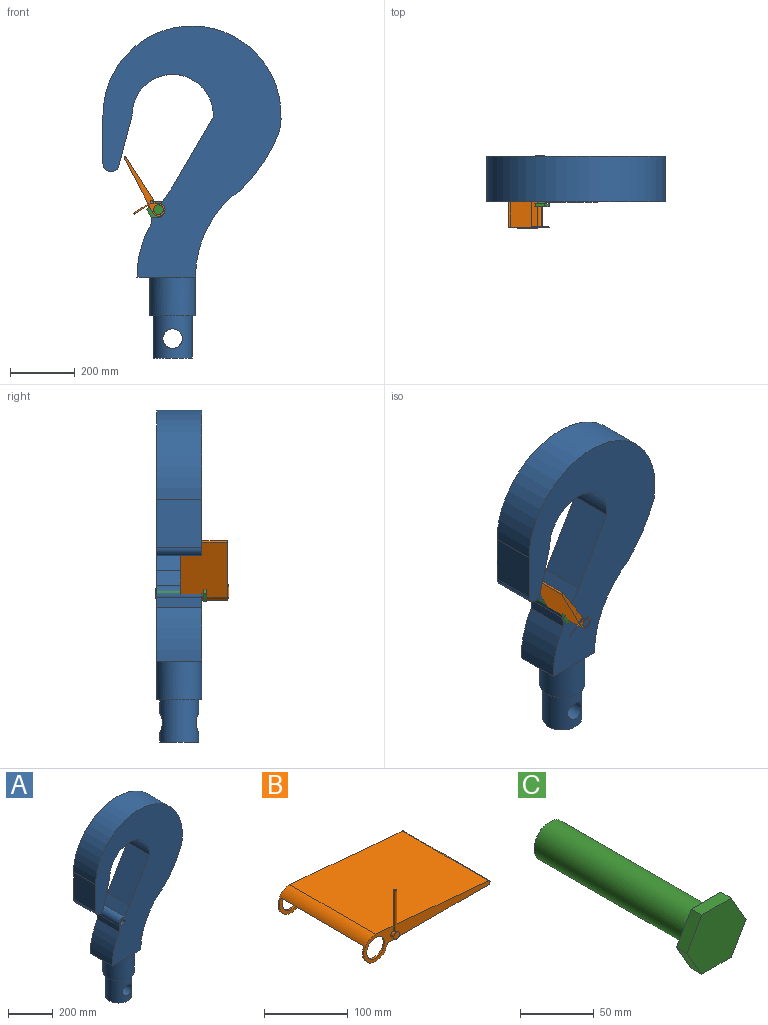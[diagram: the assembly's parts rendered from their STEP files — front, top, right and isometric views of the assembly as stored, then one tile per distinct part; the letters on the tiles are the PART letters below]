
ASSEMBLY  parts=3 mates=2
PART A: 26 faces, bbox 550x140x1025 mm
  f0: cylinder r=60mm len=130mm, axis (0,0,1), area 43158mm2, adj f2,f3,f24
  f1: cylinder r=70mm len=140mm, axis (0,0,1), area 52778.8mm2, adj f2,f4,f5
  f2: plane 140x140mm, normal (0,0,-1), area 4084.1mm2, adj f0,f1
  f3: plane 120x120mm, normal (0,0,-1), area 11309.7mm2, adj f0
  f4: plane 140x110mm, normal (0,0,-1), area 7703.1mm2, adj f1,f15,f22,f23
  f5: plane 140x70.62mm, normal (0,0,-1), area 2190.5mm2, adj f1,f16,f22,f23
  f6: cylinder r=125mm len=140mm, axis (0,1,0), area 24676.8mm2, adj f7,f21,f22,f23
  f7: plane 140x1.56mm, normal (1,0,0), area 218.2mm2, adj f6,f8,f22,f23
  f8: plane 140x40mm, normal (0,0,-1), area 5600mm2, adj f7,f9,f22,f23
  f9: plane 140x1.56mm, normal (-1,0,0), area 218.2mm2, adj f8,f10,f22,f23
  f10: cylinder r=125mm len=140mm, axis (0,1,0), area 25571.4mm2, adj f9,f11,f22,f23
  f11: plane 215.2x140mm, normal (-0.86,0,0.5), area 34830.4mm2, adj f10,f12,f22,f23
  f12: plane 140x45.84mm, normal (-0.82,0,0.57), area 7800mm2, adj f11,f13,f22,f23
  f13: cylinder r=30mm len=140mm, axis (0,1,0), area 8131.9mm2, adj f12,f14,f22,f23
  f14: plane 140x32.55mm, normal (-1,0,0), area 4556.4mm2, adj f13,f15,f22,f23
  f15: cylinder r=330mm len=164.53mm, axis (0,1,0), area 24113.8mm2, adj f4,f14,f22,f23
  f16: cylinder r=330mm len=272.73mm, axis (0,1,0), area 44941.8mm2, adj f5,f17,f22,f23
  f17: cylinder r=516.11mm len=181.02mm, axis (0,1,0), area 30341mm2, adj f16,f18,f22,f23
  f18: cylinder r=275mm len=550mm, axis (0,1,0), area 127458mm2, adj f17,f19,f22,f23
  f19: plane 150x140mm, normal (-1,0,0), area 21000mm2, adj f18,f20,f22,f23
  f20: cylinder r=25mm len=140mm, axis (0,1,0), area 10101.7mm2, adj f19,f21,f22,f23
  f21: plane 156.32x140mm, normal (0.97,0,-0.25), area 22617.7mm2, adj f6,f20,f22,f23
  f22: plane 775x550mm, normal (0,-1,0), area 209087.8mm2, adj f4,f5,f6,f7,f8,f9,f10,f11
  f23: plane 775x550mm, normal (0,1,0), area 209087.8mm2, adj f4,f5,f6,f7,f8,f9,f10,f11
  f24: cylinder r=30mm len=120mm, axis (0,1,0), area 21131.3mm2, adj f0
  f25: cylinder r=15mm len=140mm, axis (0,-1,0), area 13194.7mm2, adj f22,f23
PART B: 18 faces, bbox 213x150x90 mm
  f0: cylinder r=5mm len=10mm, axis (0,1,0), area 137.5mm2, adj f6,f13,f15,f16
  f1: plane 170.3x145mm, normal (0,0,-1), area 17661.4mm2, adj f3,f4,f6,f7,f10,f11,f12
  f2: cylinder r=15mm len=145mm, axis (0,1,0), area 4003.7mm2, adj f6,f7,f8,f9,f10,f11
  f3: cylinder r=20mm len=145mm, axis (0,1,0), area 3350.9mm2, adj f1,f5,f6,f7,f8,f10,f11
  f4: cylinder r=3mm len=145mm, axis (0,1,0), area 1317.6mm2, adj f1,f5,f6,f7
  f5: plane 190.53x145mm, normal (0.09,0,1), area 27736mm2, adj f3,f4,f6,f7
  f6: plane 213x40mm, normal (0,-1,0), area 2865.1mm2, adj f0,f1,f2,f3,f4,f5
  f7: plane 213x40mm, normal (0,1,0), area 2943.6mm2, adj f1,f2,f3,f4,f5
  f8: plane 140x6.14mm, normal (0,0,-1), area 859.6mm2, adj f2,f3,f10,f11
  f9: plane 140x58.82mm, normal (0,0,-1), area 8234.8mm2, adj f2,f10,f11,f12
  f10: plane 90x30mm, normal (0,-1,0), area 1040.4mm2, adj f1,f2,f3,f8,f9,f12
  f11: plane 90x30mm, normal (0,1,0), area 1040.4mm2, adj f1,f2,f3,f8,f9,f12
  f12: plane 140x13mm, normal (-1,0,0), area 1819.9mm2, adj f1,f9,f10,f11
  f13: plane 10x10mm, normal (0,-1,0), area 78.5mm2, adj f0
  f14: plane 3.5x3.5mm, normal (0,0,-1), area 9.6mm2, adj f15
  f15: cylinder r=1.75mm len=3.5mm, axis (0,0,-1), area 4.5mm2, adj f0,f14
  f16: cylinder r=1.75mm len=60.2mm, axis (0,0,-1), area 658.9mm2, adj f0,f17
  f17: plane 3.5x3.5mm, normal (0,0,1), area 9.6mm2, adj f16
PART C: 10 faces, bbox 56.7x160x49.1 mm
  f0: cylinder r=15mm len=150mm, axis (0,1,0), area 14137.2mm2, adj f1,f9
  f1: plane 30x30mm, normal (0,1,0), area 706.9mm2, adj f0
  f2: plane 28.37x10mm, normal (0,0,1), area 283.7mm2, adj f3,f7,f8,f9
  f3: plane 24.57x14.18mm, normal (-0.87,0,0.5), area 283.7mm2, adj f2,f4,f8,f9
  f4: plane 24.57x14.18mm, normal (-0.87,0,-0.5), area 283.7mm2, adj f3,f5,f8,f9
  f5: plane 28.37x10mm, normal (0,0,-1), area 283.7mm2, adj f4,f6,f8,f9
  f6: plane 24.57x14.18mm, normal (0.87,0,-0.5), area 283.7mm2, adj f5,f7,f8,f9
  f7: plane 24.57x14.18mm, normal (0.87,0,0.5), area 283.7mm2, adj f2,f6,f8,f9
  f8: plane 56.74x49.14mm, normal (0,-1,0), area 2091mm2, adj f2,f3,f4,f5,f6,f7
  f9: plane 56.74x49.14mm, normal (0,1,0), area 1384.2mm2, adj f0,f2,f3,f4,f5,f6,f7
PLACE A t=(-743.29,-82.64,-272.84)mm
PLACE B rot(axis=(0,-1,0),122.7deg) t=(-770.47,-174.49,-78.71)mm
PLACE C t=(-794.43,-82.64,-65.06)mm
MATE cylindrical B.f2 <-> A.f25  axis (0,1,0) through (-786.77,-228.53,-65.06)mm
MATE pin_slot C.f0 <-> A.f25  axis (0,1,0) through (-794.43,-82.64,-65.06)mm
